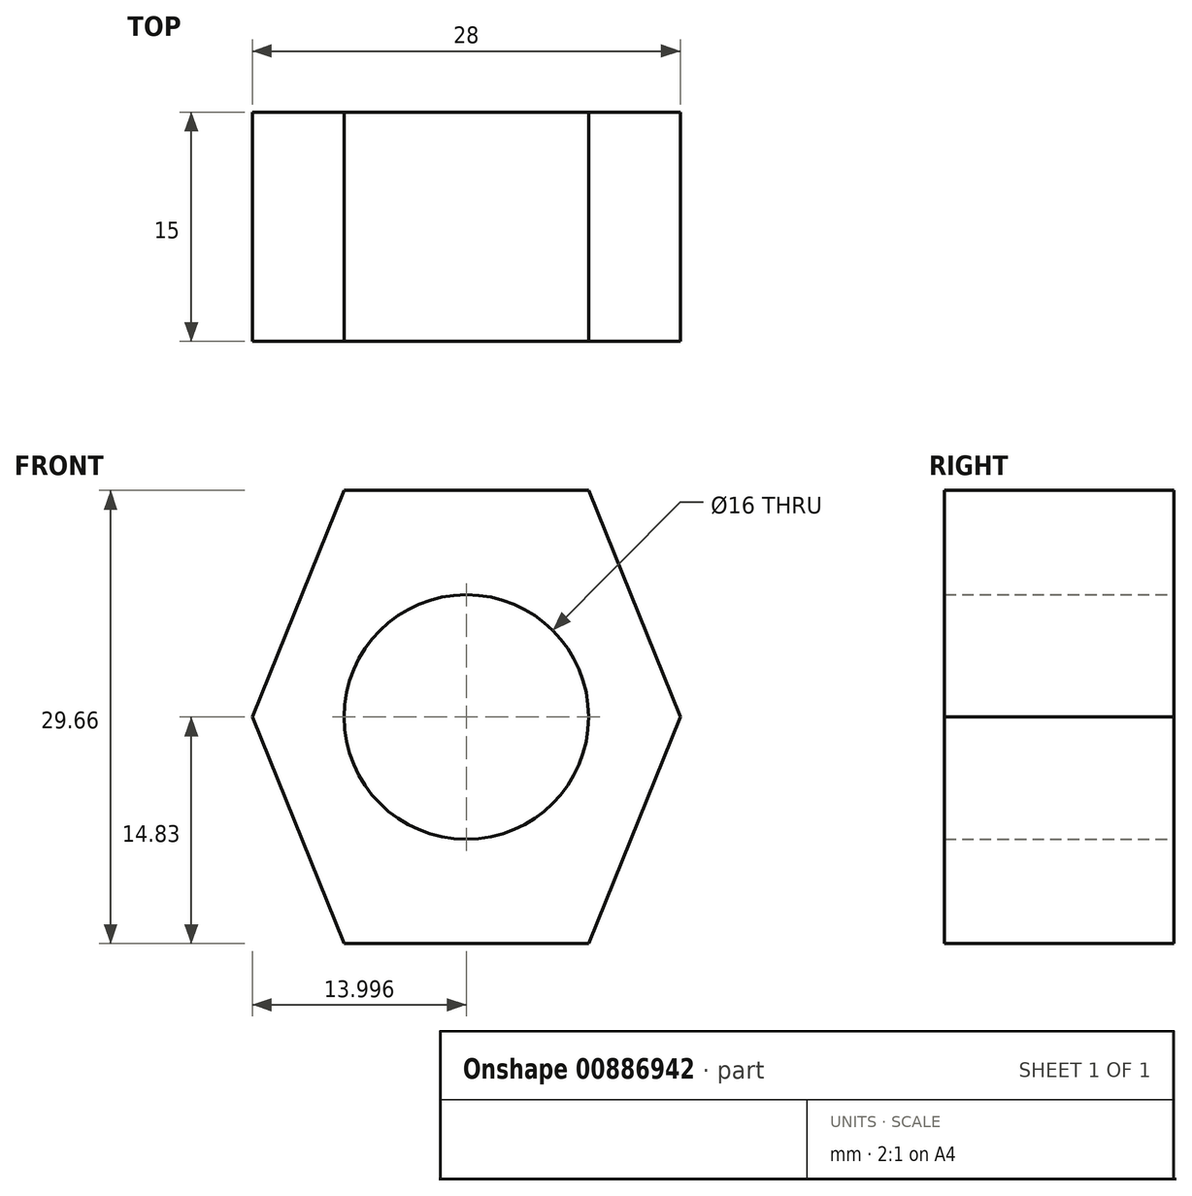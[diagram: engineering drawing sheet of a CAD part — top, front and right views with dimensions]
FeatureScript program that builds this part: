
annotation { "Feature Type Name" : "Feature", "Feature Type Description" : "" }
export const myFeature = defineFeature(function(context is Context, id is Id, definition is map)
    precondition{}
    {
        {
            var Q0;
            Q0=qCreatedBy(makeId("Front.planeOp"),FACE);
            var sketch = newSketch(context, id + "F0", { "sketchPlane" : qUnion([Q0])});
            skLineSegment(sketch, "E0", {"start": v(-8.25, 0) * mm, "end": v(-2.25, 14.83) * mm});
            skLineSegment(sketch, "E1", {"start": v(-2.25, 14.83) * mm, "end": v(13.75, 14.83) * mm});
            skLineSegment(sketch, "E2", {"start": v(13.75, 14.83) * mm, "end": v(19.75, 0) * mm});
            skArc(sketch, "E3", {"start": v(13.75, 0) * mm, "mid": v(5.75, 8) * mm, "end": v(-2.25, 0) * mm});
            skLineSegment(sketch, "E4", {"start": v(-8.25, 0) * mm, "end": v(-2.25, -14.83) * mm});
            skLineSegment(sketch, "E5", {"start": v(-2.25, -14.83) * mm, "end": v(13.75, -14.83) * mm});
            skLineSegment(sketch, "E6", {"start": v(13.75, -14.83) * mm, "end": v(19.75, 0) * mm});
            skArc(sketch, "E7", {"start": v(13.75, 0) * mm, "mid": v(5.75, -8) * mm, "end": v(-2.25, 0) * mm});
            skSolve(sketch);
        }
        {
            var Q0;
            Q0=makeQuery(id+"F0.imprint","IMPRINT",FACE,{"disambiguationData":[TD([[makeQuery(id+"F0.imprint","IMPRINT",EDGE,{"derivedFrom":sQuery(id+"F0.wireOp",EDGE,"E0")}),-1.0]])]});
            extrude(context, id + "F1", {"entities" : qUnion([Q0]), "depth" : 15 * mm, "offsetDistance" : 25 * mm});
        }
    });
